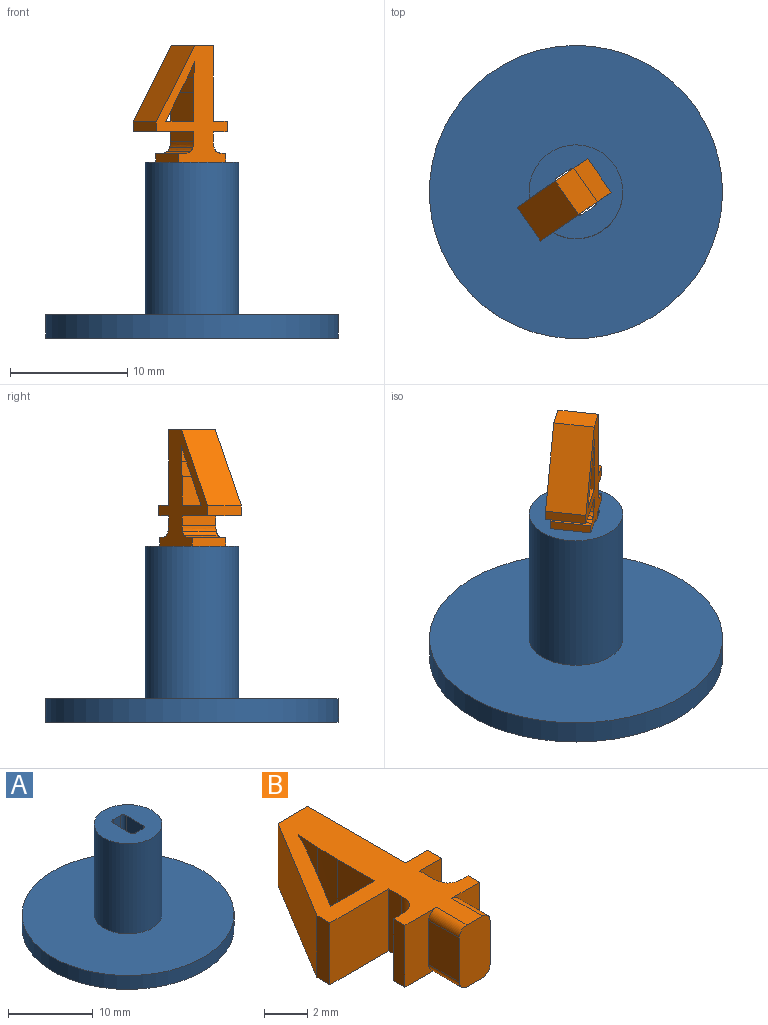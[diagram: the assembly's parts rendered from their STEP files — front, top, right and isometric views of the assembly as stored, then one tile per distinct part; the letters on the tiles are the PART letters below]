
ASSEMBLY  parts=2 mates=1
PART A: 13 faces, bbox 25x25x15 mm
  f0: cylinder r=12.5mm len=25mm, axis (0,0,-1), area 157.1mm2, adj f1,f2
  f1: plane 25x25mm, normal (0,0,1), area 440.6mm2, adj f0,f7
  f2: plane 25x25mm, normal (0,0,-1), area 482.7mm2, adj f0,f3,f4,f5,f6,f9,f10,f11
  f3: plane 15x2.8mm, normal (-1,0,0), area 42mm2, adj f2,f8,f9,f12
  f4: plane 15x1.2mm, normal (0,1,0), area 18mm2, adj f2,f8,f9,f10
  f5: plane 15x2.8mm, normal (1,0,0), area 42mm2, adj f2,f8,f10,f11
  f6: plane 15x1.2mm, normal (0,-1,0), area 18mm2, adj f2,f8,f11,f12
  f7: cylinder r=4mm len=13mm, axis (0,0,-1), area 326.7mm2, adj f1,f8
  f8: plane 8x8mm, normal (0,0,1), area 42.1mm2, adj f3,f4,f5,f6,f7,f9,f10,f11
  f9: cylinder r=0.5mm len=15mm, axis (0,0,-1), area 11.8mm2, adj f2,f3,f4,f8
  f10: cylinder r=0.5mm len=15mm, axis (0,0,1), area 11.8mm2, adj f2,f4,f5,f8
  f11: cylinder r=0.5mm len=15mm, axis (0,0,-1), area 11.8mm2, adj f2,f5,f6,f8
  f12: cylinder r=0.5mm len=15mm, axis (0,0,1), area 11.8mm2, adj f2,f3,f6,f8
PART B: 42 faces, bbox 7.3x11.9x3.5 mm
  f0: extruded ~3.5x1.32mm, area 4.6mm2, adj f1,f35,f36,f37
  f1: plane 3.5x2.43mm, normal (-1,0,0), area 8.5mm2, adj f0,f2,f36,f37
  f2: plane 3.5x2.88mm, normal (0,1,0), area 10.1mm2, adj f1,f3,f36,f37
  f3: plane 3.5x3.1mm, normal (0.86,-0.52,0), area 12.7mm2, adj f2,f4,f36,f37
  f4: extruded ~3.5x0.4mm, area 1.6mm2, adj f3,f5,f36,f37
  f5: extruded ~3.5x0.57mm, area 2.3mm2, adj f4,f6,f36,f37
  f6: extruded ~3.5x0.59mm, area 2.3mm2, adj f5,f7,f36,f37
  f7: extruded ~3.5x0.45mm, area 1.7mm2, adj f6,f35,f36,f37
  f8: plane 2.5x2mm, normal (1,0,0), area 5mm2, adj f9,f34,f38,f40
  f9: plane 3.5x1.81mm, normal (0,-1,0), area 4.7mm2, adj f8,f10,f36,f37,f38,f40
  f10: plane 3.5x0.74mm, normal (1,0,0), area 2.6mm2, adj f9,f11,f36,f37
  f11: plane 3.5x0.18mm, normal (0,1,0), area 0.6mm2, adj f10,f12,f36,f37
  f12: extruded ~3.5x0.44mm, area 1.6mm2, adj f11,f13,f36,f37
  f13: extruded ~3.5x0.36mm, area 1.4mm2, adj f12,f14,f36,f37
  f14: extruded ~3.5x0.3mm, area 1.4mm2, adj f13,f15,f36,f37
  f15: extruded ~3.5x0.52mm, area 1.9mm2, adj f14,f16,f36,f37
  f16: plane 3.5x0.85mm, normal (1,0,0), area 3mm2, adj f15,f17,f36,f37
  f17: plane 3.5x1.44mm, normal (0,-1,0), area 5.1mm2, adj f16,f18,f36,f37
  f18: plane 3.5x0.92mm, normal (1,0,0), area 3.2mm2, adj f17,f19,f36,f37
  f19: plane 3.5x1.44mm, normal (0,1,0), area 5.1mm2, adj f18,f20,f36,f37
  f20: plane 6.42x3.5mm, normal (1,0,0), area 22.5mm2, adj f19,f21,f36,f37
  f21: plane 3.5x1.93mm, normal (0,1,0), area 6.8mm2, adj f20,f22,f36,f37
  f22: plane 6.48x3.94mm, normal (-0.85,0.52,0), area 26.6mm2, adj f21,f23,f36,f37
  f23: plane 3.5x0.85mm, normal (-1,0,0), area 3mm2, adj f22,f24,f36,f37
  f24: plane 3.85x3.5mm, normal (0,-1,0), area 13.5mm2, adj f23,f25,f36,f37
  f25: plane 3.5x0.85mm, normal (-1,0,0), area 3mm2, adj f24,f26,f36,f37
  f26: extruded ~3.5x0.52mm, area 1.9mm2, adj f25,f27,f36,f37
  f27: extruded ~3.5x0.3mm, area 1.4mm2, adj f26,f28,f36,f37
  f28: extruded ~3.5x0.36mm, area 1.4mm2, adj f27,f29,f36,f37
  f29: extruded ~3.5x0.45mm, area 1.6mm2, adj f28,f30,f36,f37
  f30: plane 3.5x0.39mm, normal (0,1,0), area 1.4mm2, adj f29,f31,f36,f37
  f31: plane 3.5x0.74mm, normal (-1,0,0), area 2.6mm2, adj f30,f32,f36,f37
  f32: plane 3.5x2.06mm, normal (0,-1,0), area 5.6mm2, adj f31,f33,f36,f37,f39,f41
  f33: plane 2.5x2mm, normal (-1,0,0), area 5mm2, adj f32,f34,f39,f41
  f34: plane 3.5x2mm, normal (0,-1,0), area 6.8mm2, adj f8,f33,f36,f37,f38,f39,f40,f41
  f35: extruded ~3.5x1.36mm, area 4.8mm2, adj f0,f7,f36,f37
  f36: plane 11.92x7.32mm, normal (0,0,1), area 34.3mm2, adj f0,f1,f2,f3,f4,f5,f6,f7
  f37: plane 11.92x7.32mm, normal (0,0,-1), area 34.3mm2, adj f0,f1,f2,f3,f4,f5,f6,f7
  f38: cylinder r=0.5mm len=2mm, axis (0,1,0), area 1.6mm2, adj f8,f9,f34,f37
  f39: cylinder r=0.5mm len=2mm, axis (0,-1,0), area 1.6mm2, adj f32,f33,f34,f37
  f40: cylinder r=0.5mm len=2mm, axis (0,-1,0), area 1.6mm2, adj f8,f9,f34,f36
  f41: cylinder r=0.5mm len=2mm, axis (0,1,0), area 1.6mm2, adj f32,f33,f34,f36
PLACE A rot(axis=(0,0,1),34.6deg) t=(0.54,-0.05,0)mm
PLACE B rot(axis=(0.92,0.28,0.28),95.1deg) t=(38.46,28.21,-23.95)mm
MATE slider B.f34 <-> A.f7  axis (0,0,-1) through (0.54,-0.05,13)mm
